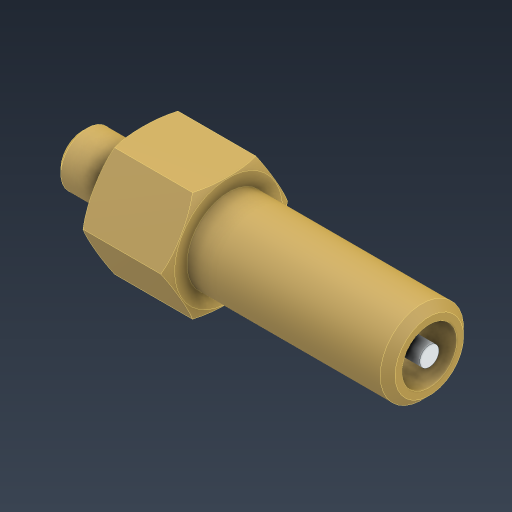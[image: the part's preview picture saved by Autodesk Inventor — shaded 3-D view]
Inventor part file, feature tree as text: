
AUTODESK INVENTOR PART (.ipt)
format: ipt  version: 2024.3 (Build 283343000, 343)  size: 240,640 bytes
history: native  units: in
note: dims shown in document units (in); Inventor stores cm internally (conversion verified against a paired STEP export)
features: other x3, revolve x1
ambient origin geometry x8: Origin, YZ Plane, XZ Plane, XY Plane, X Axis, Y Axis, Z Axis, Center Point
bodies: Solid1 (feature_tree), Solid2 (feature_tree), Solid3 (feature_tree)
feature tree (4):
  other  "Schrader Valve1"
  revolve  "Revolve2"  [1 undecoded]
  other  "Boss-Extrude1"
  other  "Cut-Revolve2"
note: 1 required parameter value undecoded (feature->parameter linkage not recoverable at this tier; creation-order binding heuristic only, values carry confidence <= 0.55)
